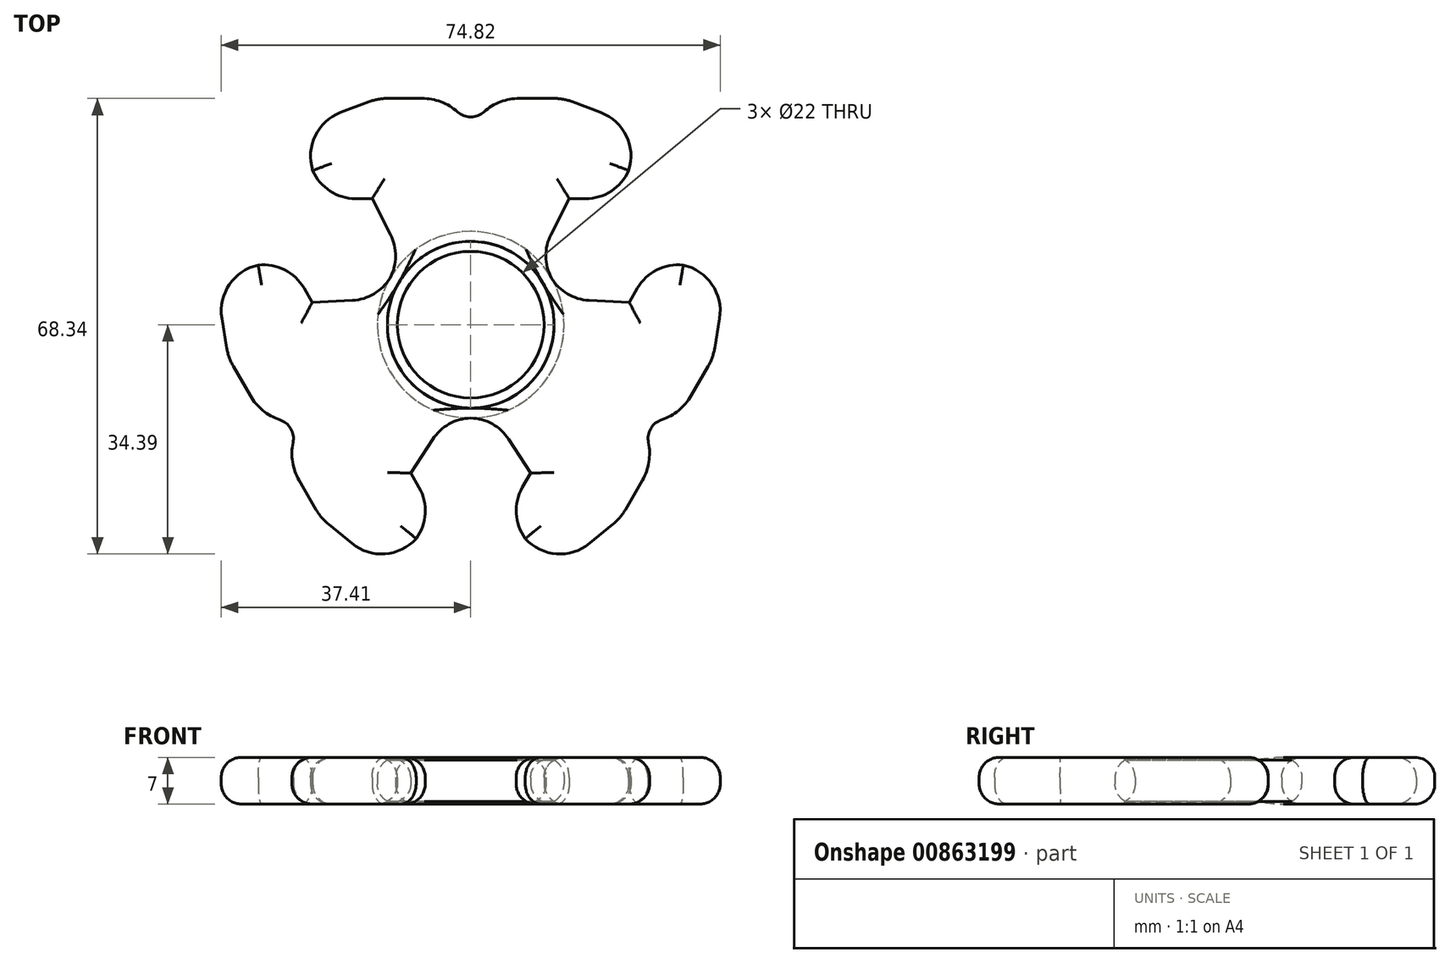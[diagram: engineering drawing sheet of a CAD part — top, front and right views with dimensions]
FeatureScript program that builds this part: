
annotation { "Feature Type Name" : "Feature", "Feature Type Description" : "" }
export const myFeature = defineFeature(function(context is Context, id is Id, definition is map)
    precondition{}
    {
        {
            var Q0;
            Q0=qCreatedBy(makeId("Top.planeOp"),FACE);
            var sketch = newSketch(context, id + "F0", { "sketchPlane" : qUnion([Q0])});
            skCircle(sketch, "E0", {"center": v(0, 0) * mm, "radius": 11 * mm});
            skCircle(sketch, "E1.0", {"center": v(0, 0) * mm, "radius": 14 * mm});
            skLineSegment(sketch, "E2", {"start": v(10.08, 9.71) * mm, "end": v(14.77, 18.9) * mm});
            skLineSegment(sketch, "E3", {"start": v(14.77, 18.9) * mm, "end": v(22.1, 18.9) * mm});
            skLineSegment(sketch, "E4", {"start": v(22.1, 18.9) * mm, "end": v(26.05, 29.36) * mm});
            skLineSegment(sketch, "E5", {"start": v(26.05, 29.36) * mm, "end": v(13.89, 33.95) * mm});
            skLineSegment(sketch, "E6", {"start": v(13.89, 33.95) * mm, "end": v(3.2, 33.95) * mm});
            skLineSegment(sketch, "E7", {"start": v(3.2, 33.95) * mm, "end": v(0, 26.85) * mm});
            skLineSegment(sketch, "E8.MirrorCS", {"start": v(-3.2, 33.95) * mm, "end": v(0, 26.85) * mm});
            skLineSegment(sketch, "E9.MirrorCS", {"start": v(-10.08, 9.71) * mm, "end": v(-14.77, 18.9) * mm});
            skLineSegment(sketch, "E10.MirrorCS", {"start": v(-22.1, 18.9) * mm, "end": v(-26.05, 29.36) * mm});
            skLineSegment(sketch, "E11.MirrorCS", {"start": v(-26.05, 29.36) * mm, "end": v(-13.89, 33.95) * mm});
            skLineSegment(sketch, "E12.MirrorCS", {"start": v(-13.89, 33.95) * mm, "end": v(-3.2, 33.95) * mm});
            skLineSegment(sketch, "E13.MirrorCS", {"start": v(-14.77, 18.9) * mm, "end": v(-22.1, 18.9) * mm});
            skSolve(sketch);
        }
        {
            var Q0;
            {var subQ1=sQuery(id+"F0.wireOp",EDGE,"E2");Q0=makeQuery(id+"F0.imprint","IMPRINT",FACE,{"disambiguationData":[TD([[makeQuery(id+"F0.imprint","IMPRINT",EDGE,{"derivedFrom":subQ1}),1.0]])]});}
            var Q1;
            Q1=makeQuery(id+"F0.imprint","IMPRINT",FACE,{"disambiguationData":[TD([[makeQuery(id+"F0.imprint","IMPRINT",EDGE,{"derivedFrom":sQuery(id+"F0.wireOp",EDGE,"E0")}),-1.0]])]});
            extrude(context, id + "F1", {"entities" : qUnion([Q0, Q1]), "depth" : 7 * mm, "offsetDistance" : 25 * mm});
        }
        {
            var Q0;
            Q0=makeQuery(id+"F1.opExtrude","SWEPT_EDGE",EDGE,{"disambiguationData":[OSD([sQuery(id+"F0.wireOp",EDGE,"E10.MirrorCS"),sQuery(id+"F0.wireOp",EDGE,"E11.MirrorCS")])]});
            var Q1;
            Q1=makeQuery(id+"F1.opExtrude","SWEPT_EDGE",EDGE,{"disambiguationData":[OSD([sQuery(id+"F0.wireOp",EDGE,"E1.0"),sQuery(id+"F0.wireOp",EDGE,"E9.MirrorCS")])]});
            var Q2;
            Q2=makeQuery(id+"F1.opExtrude","SWEPT_EDGE",EDGE,{"disambiguationData":[OSD([sQuery(id+"F0.wireOp",EDGE,"E10.MirrorCS"),sQuery(id+"F0.wireOp",EDGE,"E13.MirrorCS")])]});
            var Q3;
            Q3=makeQuery(id+"F1.opExtrude","SWEPT_EDGE",EDGE,{"disambiguationData":[OSD([sQuery(id+"F0.wireOp",EDGE,"E1.0"),sQuery(id+"F0.wireOp",EDGE,"E2")])]});
            var Q4;
            Q4=makeQuery(id+"F1.opExtrude","SWEPT_EDGE",EDGE,{"disambiguationData":[OSD([sQuery(id+"F0.wireOp",EDGE,"E4"),sQuery(id+"F0.wireOp",EDGE,"E5")])]});
            var Q5;
            Q5=makeQuery(id+"F1.opExtrude","SWEPT_EDGE",EDGE,{"disambiguationData":[OSD([sQuery(id+"F0.wireOp",EDGE,"E3"),sQuery(id+"F0.wireOp",EDGE,"E4")])]});
            fillet(context, id + "F2", {"entities" : qUnion([Q0, Q1, Q2, Q3, Q4, Q5]), "radius" : 7 * mm, "tangentPropagation" : true, "allowEdgeOverflow" : false});
        }
        {
            var Q0;
            Q0=makeQuery(id+"F1.opExtrude","SWEPT_EDGE",EDGE,{"disambiguationData":[OSD([sQuery(id+"F0.wireOp",EDGE,"E7"),sQuery(id+"F0.wireOp",EDGE,"E8.MirrorCS")])]});
            fillet(context, id + "F3", {"entities" : qUnion([Q0]), "radius" : 3 * mm, "tangentPropagation" : true, "allowEdgeOverflow" : false});
        }
        {
            var Q0;
            Q0=makeQuery(id+"F1.opExtrude","SWEPT_EDGE",EDGE,{"disambiguationData":[OSD([sQuery(id+"F0.wireOp",EDGE,"E6"),sQuery(id+"F0.wireOp",EDGE,"E7")])]});
            var Q1;
            Q1=makeQuery(id+"F1.opExtrude","SWEPT_EDGE",EDGE,{"disambiguationData":[OSD([sQuery(id+"F0.wireOp",EDGE,"E8.MirrorCS"),sQuery(id+"F0.wireOp",EDGE,"E12.MirrorCS")])]});
            var Q2;
            Q2=makeQuery(id+"F1.opExtrude","SWEPT_EDGE",EDGE,{"disambiguationData":[OSD([sQuery(id+"F0.wireOp",EDGE,"E11.MirrorCS"),sQuery(id+"F0.wireOp",EDGE,"E12.MirrorCS")])]});
            var Q3;
            Q3=makeQuery(id+"F1.opExtrude","SWEPT_EDGE",EDGE,{"disambiguationData":[OSD([sQuery(id+"F0.wireOp",EDGE,"E5"),sQuery(id+"F0.wireOp",EDGE,"E6")])]});
            fillet(context, id + "F4", {"entities" : qUnion([Q0, Q1, Q2, Q3]), "radius" : 8 * mm, "tangentPropagation" : true, "allowEdgeOverflow" : false});
        }
        {
            var Q0;
            Q0=makeQuery(id+"F1.opExtrude","CAP_FACE",FACE,{"disambiguationData":[OSD([sQuery(id+"F0.wireOp",EDGE,"E0"),sQuery(id+"F0.wireOp",EDGE,"E1.0"),sQuery(id+"F0.wireOp",EDGE,"E2"),sQuery(id+"F0.wireOp",EDGE,"E3"),sQuery(id+"F0.wireOp",EDGE,"E4"),sQuery(id+"F0.wireOp",EDGE,"E5"),sQuery(id+"F0.wireOp",EDGE,"E6"),sQuery(id+"F0.wireOp",EDGE,"E7"),sQuery(id+"F0.wireOp",EDGE,"E8.MirrorCS"),sQuery(id+"F0.wireOp",EDGE,"E9.MirrorCS"),sQuery(id+"F0.wireOp",EDGE,"E10.MirrorCS"),sQuery(id+"F0.wireOp",EDGE,"E11.MirrorCS"),sQuery(id+"F0.wireOp",EDGE,"E12.MirrorCS"),sQuery(id+"F0.wireOp",EDGE,"E13.MirrorCS")])],"isStart":false});
            var Q1;
            Q1=makeQuery(id+"F1.opExtrude","CAP_FACE",FACE,{"disambiguationData":[OSD([sQuery(id+"F0.wireOp",EDGE,"E0"),sQuery(id+"F0.wireOp",EDGE,"E1.0"),sQuery(id+"F0.wireOp",EDGE,"E2"),sQuery(id+"F0.wireOp",EDGE,"E3"),sQuery(id+"F0.wireOp",EDGE,"E4"),sQuery(id+"F0.wireOp",EDGE,"E5"),sQuery(id+"F0.wireOp",EDGE,"E6"),sQuery(id+"F0.wireOp",EDGE,"E7"),sQuery(id+"F0.wireOp",EDGE,"E8.MirrorCS"),sQuery(id+"F0.wireOp",EDGE,"E9.MirrorCS"),sQuery(id+"F0.wireOp",EDGE,"E10.MirrorCS"),sQuery(id+"F0.wireOp",EDGE,"E11.MirrorCS"),sQuery(id+"F0.wireOp",EDGE,"E12.MirrorCS"),sQuery(id+"F0.wireOp",EDGE,"E13.MirrorCS")])],"isStart":true});
            fillet(context, id + "F5", {"entities" : qUnion([Q0, Q1]), "radius" : 3 * mm, "tangentPropagation" : true, "allowEdgeOverflow" : false});
        }
        {
            var Q0;
            Q0=makeQuery(id+"F1.opExtrude","SWEPT_BODY",BODY,{"disambiguationData":[OSD([sQuery(id+"F0.wireOp",EDGE,"E0"),sQuery(id+"F0.wireOp",EDGE,"E1.0"),sQuery(id+"F0.wireOp",EDGE,"E2"),sQuery(id+"F0.wireOp",EDGE,"E3"),sQuery(id+"F0.wireOp",EDGE,"E4"),sQuery(id+"F0.wireOp",EDGE,"E5"),sQuery(id+"F0.wireOp",EDGE,"E6"),sQuery(id+"F0.wireOp",EDGE,"E7"),sQuery(id+"F0.wireOp",EDGE,"E8.MirrorCS"),sQuery(id+"F0.wireOp",EDGE,"E9.MirrorCS"),sQuery(id+"F0.wireOp",EDGE,"E10.MirrorCS"),sQuery(id+"F0.wireOp",EDGE,"E11.MirrorCS"),sQuery(id+"F0.wireOp",EDGE,"E12.MirrorCS"),sQuery(id+"F0.wireOp",EDGE,"E13.MirrorCS")])]});
            var Q1;
            {var subQ0=sQuery(id+"F0.wireOp",EDGE,"E0");Q1=makeQuery(id+"F5.opFillet","BLEND_EDGE",EDGE,{"blendedFrom":[makeQuery(id+"F1.opExtrude","CAP_EDGE",EDGE,{"disambiguationData":[OSD([subQ0])],"isStart":true}),makeQuery(id+"F1.opExtrude","SWEPT_FACE",FACE,{"disambiguationData":[OSD([subQ0])]})],"blendedInto":[makeQuery(id+"F1.opExtrude","SWEPT_FACE",FACE,{"disambiguationData":[OSD([subQ0])]})]});}
            circularPattern(context, id + "F6", {"entities" : qUnion([Q0]), "axis" : qUnion([Q1]), "angle" : 360 * degree, "instanceCount" : 3, "equalSpace" : true});
        }
    });
